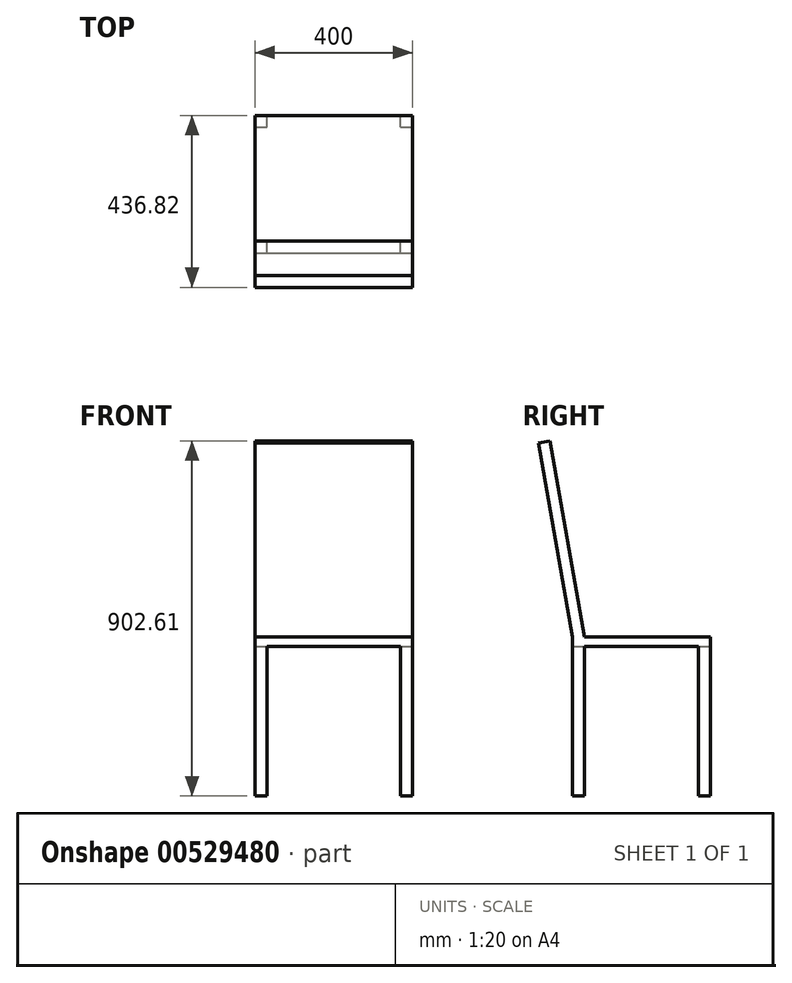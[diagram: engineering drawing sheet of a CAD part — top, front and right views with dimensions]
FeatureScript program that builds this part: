
annotation { "Feature Type Name" : "Feature", "Feature Type Description" : "" }
export const myFeature = defineFeature(function(context is Context, id is Id, definition is map)
    precondition{}
    {
        {
            var Q0;
            Q0=qCreatedBy(makeId("Top.planeOp"),FACE);
            var sketch = newSketch(context, id + "F0", { "sketchPlane" : qUnion([Q0])});
            skLineSegment(sketch, "E0.bottom", {"start": v(0, 0) * mm, "end": v(400, 0) * mm});
            skLineSegment(sketch, "E0.top", {"start": v(0, 350) * mm, "end": v(400, 350) * mm});
            skLineSegment(sketch, "E0.left", {"start": v(0, 0) * mm, "end": v(0, 350) * mm});
            skLineSegment(sketch, "E0.right", {"start": v(400, 0) * mm, "end": v(400, 350) * mm});
            skSolve(sketch);
        }
        {
            var Q0;
            Q0=makeQuery(id+"F0.imprint","IMPRINT",FACE,{"disambiguationData":[TD([[makeQuery(id+"F0.imprint","IMPRINT",EDGE,{"derivedFrom":sQuery(id+"F0.wireOp",EDGE,"E0.bottom")}),1.0]])]});
            extrude(context, id + "F1", {"entities" : qUnion([Q0]), "depth" : 25 * mm, "offsetDistance" : 25 * mm});
        }
        {
            var Q0;
            Q0=makeQuery(id+"F1.opExtrude","CAP_FACE",FACE,{"disambiguationData":[OSD([sQuery(id+"F0.wireOp",EDGE,"E0.bottom"),sQuery(id+"F0.wireOp",EDGE,"E0.top"),sQuery(id+"F0.wireOp",EDGE,"E0.left"),sQuery(id+"F0.wireOp",EDGE,"E0.right")])],"isStart":true});
            var sketch = newSketch(context, id + "F2", { "sketchPlane" : qUnion([Q0])});
            skLineSegment(sketch, "E1.bottom", {"start": v(0, 0) * mm, "end": v(30, 0) * mm});
            skLineSegment(sketch, "E1.top", {"start": v(0, -30) * mm, "end": v(30, -30) * mm});
            skLineSegment(sketch, "E1.left", {"start": v(0, 0) * mm, "end": v(0, -30) * mm});
            skLineSegment(sketch, "E1.right", {"start": v(30, 0) * mm, "end": v(30, -30) * mm});
            skLineSegment(sketch, "E2.0.1.0", {"start": v(0, -320) * mm, "end": v(30, -320) * mm});
            skLineSegment(sketch, "E2.0.1.1", {"start": v(0, -350) * mm, "end": v(30, -350) * mm});
            skLineSegment(sketch, "E2.0.1.2", {"start": v(0, -320) * mm, "end": v(0, -350) * mm});
            skLineSegment(sketch, "E2.0.1.3", {"start": v(30, -320) * mm, "end": v(30, -350) * mm});
            skLineSegment(sketch, "E2.1.0.0", {"start": v(370, 0) * mm, "end": v(400, 0) * mm});
            skLineSegment(sketch, "E2.1.0.1", {"start": v(370, -30) * mm, "end": v(400, -30) * mm});
            skLineSegment(sketch, "E2.1.0.2", {"start": v(370, 0) * mm, "end": v(370, -30) * mm});
            skLineSegment(sketch, "E2.1.0.3", {"start": v(400, 0) * mm, "end": v(400, -30) * mm});
            skLineSegment(sketch, "E2.1.1.0", {"start": v(370, -320) * mm, "end": v(400, -320) * mm});
            skLineSegment(sketch, "E2.1.1.1", {"start": v(370, -350) * mm, "end": v(400, -350) * mm});
            skLineSegment(sketch, "E2.1.1.2", {"start": v(370, -320) * mm, "end": v(370, -350) * mm});
            skLineSegment(sketch, "E2.1.1.3", {"start": v(400, -320) * mm, "end": v(400, -350) * mm});
            skLineSegment(sketch, "E2.direction1", {"start": v(0, -30) * mm, "end": v(370, -30) * mm, "construction": true});
            skLineSegment(sketch, "E2.direction2", {"start": v(0, -30) * mm, "end": v(0, -350) * mm, "construction": true});
            skSolve(sketch);
        }
        {
            var Q0;
            Q0=makeQuery(id+"F2.imprint","IMPRINT",FACE,{"disambiguationData":[TD([[makeQuery(id+"F2.imprint","IMPRINT",EDGE,{"derivedFrom":sQuery(id+"F2.wireOp",EDGE,"E1.bottom")}),-1.0]])]});
            var Q1;
            Q1=makeQuery(id+"F2.imprint","IMPRINT",FACE,{"disambiguationData":[TD([[makeQuery(id+"F2.imprint","IMPRINT",EDGE,{"derivedFrom":sQuery(id+"F2.wireOp",EDGE,"E2.1.0.0")}),-1.0]])]});
            var Q2;
            Q2=makeQuery(id+"F2.imprint","IMPRINT",FACE,{"disambiguationData":[TD([[makeQuery(id+"F2.imprint","IMPRINT",EDGE,{"derivedFrom":sQuery(id+"F2.wireOp",EDGE,"E2.0.1.0")}),-1.0]])]});
            var Q3;
            Q3=makeQuery(id+"F2.imprint","IMPRINT",FACE,{"disambiguationData":[TD([[makeQuery(id+"F2.imprint","IMPRINT",EDGE,{"derivedFrom":sQuery(id+"F2.wireOp",EDGE,"E2.1.1.0")}),-1.0]])]});
            extrude(context, id + "F3", {"entities" : qUnion([Q0, Q1, Q2, Q3]), "operationType" : NewBodyOperationType.ADD, "depth" : 380 * mm, "offsetDistance" : 25 * mm});
        }
        {
            var Q0;
            Q0=qCreatedBy(makeId("Right.planeOp"),FACE);
            var sketch = newSketch(context, id + "F4", { "sketchPlane" : qUnion([Q0])});
            skLineSegment(sketch, "E3", {"start": v(0, 25) * mm, "end": v(-86.82, 517.4) * mm});
            skLineSegment(sketch, "E4", {"start": v(-86.82, 517.4) * mm, "end": v(-57.28, 522.61) * mm});
            skLineSegment(sketch, "E5", {"start": v(-57.28, 522.61) * mm, "end": v(30.46, 25) * mm});
            skLineSegment(sketch, "E6", {"start": v(0, 25) * mm, "end": v(30.46, 25) * mm});
            skSolve(sketch);
        }
        {
            var Q0;
            Q0=makeQuery(id+"F4.imprint","IMPRINT",FACE,{"disambiguationData":[TD([[makeQuery(id+"F4.imprint","IMPRINT",EDGE,{"derivedFrom":sQuery(id+"F4.wireOp",EDGE,"E3")}),-1.0]])]});
            var Q1;
            Q1=makeQuery(id+"F3.boolean.opBoolean","MERGE",FACE,{"derivedFrom":[makeQuery(id+"F1.opExtrude","SWEPT_FACE",FACE,{"disambiguationData":[OSD([sQuery(id+"F0.wireOp",EDGE,"E0.right")])]}),makeQuery(id+"F3.opExtrude","SWEPT_FACE",FACE,{"disambiguationData":[OSD([sQuery(id+"F2.wireOp",EDGE,"E2.1.0.3")])]}),makeQuery(id+"F3.opExtrude","SWEPT_FACE",FACE,{"disambiguationData":[OSD([sQuery(id+"F2.wireOp",EDGE,"E2.1.1.3")])]})]});
            extrude(context, id + "F5", {"entities" : qUnion([Q0]), "operationType" : NewBodyOperationType.ADD, "endBound" : BoundingType.UP_TO_SURFACE, "depth" : 25 * mm, "endBoundEntityFace" : qUnion([Q1]), "offsetDistance" : 25 * mm});
        }
    });
